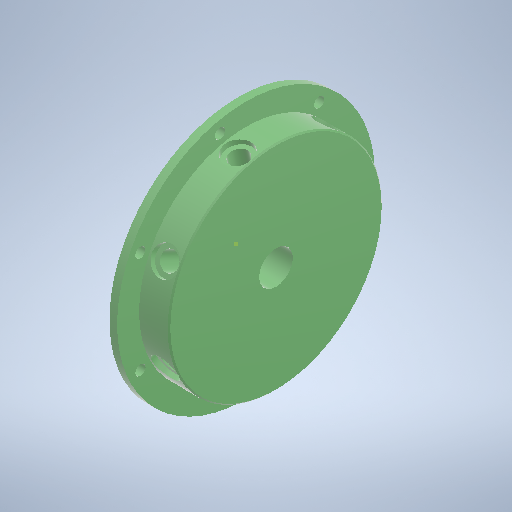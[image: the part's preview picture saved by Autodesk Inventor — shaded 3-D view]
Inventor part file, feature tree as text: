
AUTODESK INVENTOR PART (.ipt)
format: ipt  version: 2025 (Build 290162010, 162A)  size: 433,152 bytes
history: native  units: mm
features: sketch x7, pattern_circular x4, extrude x3, hole x2, revolve x1, plane x1, chamfer x1
ambient origin geometry x8: Origin, YZ Plane, XZ Plane, XY Plane, X Axis, Y Axis, Z Axis, Center Point
bodies: Volumenkörper1 (feature_tree)
feature tree (19):
  revolve  "Umdrehung1"
  hole  "Bohrung1"  [1 undecoded]
  pattern_circular  "Runde Anordnung1"  Count=10  [1 undecoded]
  extrude  "Extrusion1"  Depth=83.0mm
  plane  "Arbeitsebene2"
  hole  "Bohrung2"  [1 undecoded]
  sketch  "Skizze6"  dims[d8=4.0mm d9=6.0mm d10=4.0mm d11=2.0mm d12=90.0deg d13=8.0mm d14=0.0mm d15=70.0mm d16=360.0deg]
  extrude  "Extrusion2"  Depth=70.0mm TaperAngle=360.0deg
  extrude  "Extrusion3"  Depth=10.0mm TaperAngle=0.0deg
  pattern_circular  "Runde Anordnung2"  [2 undecoded]
  pattern_circular  "Runde Anordnung3"  [2 undecoded]
  pattern_circular  "Runde Anordnung4"  [2 undecoded]
  chamfer  "Fasen1"  Distance=17.0mm
  sketch  "Skizze1"  dims[d0=15.5mm d1=0.9mm]
  sketch  "Skizze2"  dims[d2=3.0mm d3=100.0mm]
  sketch  "Skizze3"  dims[d4=84.5mm d5=83.0mm]
  sketch  "Skizze5"  dims[d6=90.0deg d7=91.0mm]
  sketch  "Skizze7"  dims[d18=13.0mm d19=10.0mm d20=0.0mm]
  sketch  "Skizze8"  dims[d22=41.5mm d23=6.0mm d24=7.0mm d25=6.0mm d26=10.5mm d27=2.0mm d28=90.0deg d29=5.0mm d30=0.0mm d31=8.0mm d32=22.0mm d33=0.0mm d34=17.0mm d35=9.0mm d36=15.0mm d37=0.0mm d38=70.0mm d39=360.0deg d41=70.0mm d42=360.0deg d44=70.0mm d45=360.0deg d47=0.5mm d48=2.0mm d49=45.0deg]
note: 9 required parameter values undecoded (feature->parameter linkage not recoverable at this tier; creation-order binding heuristic only, values carry confidence <= 0.55)
